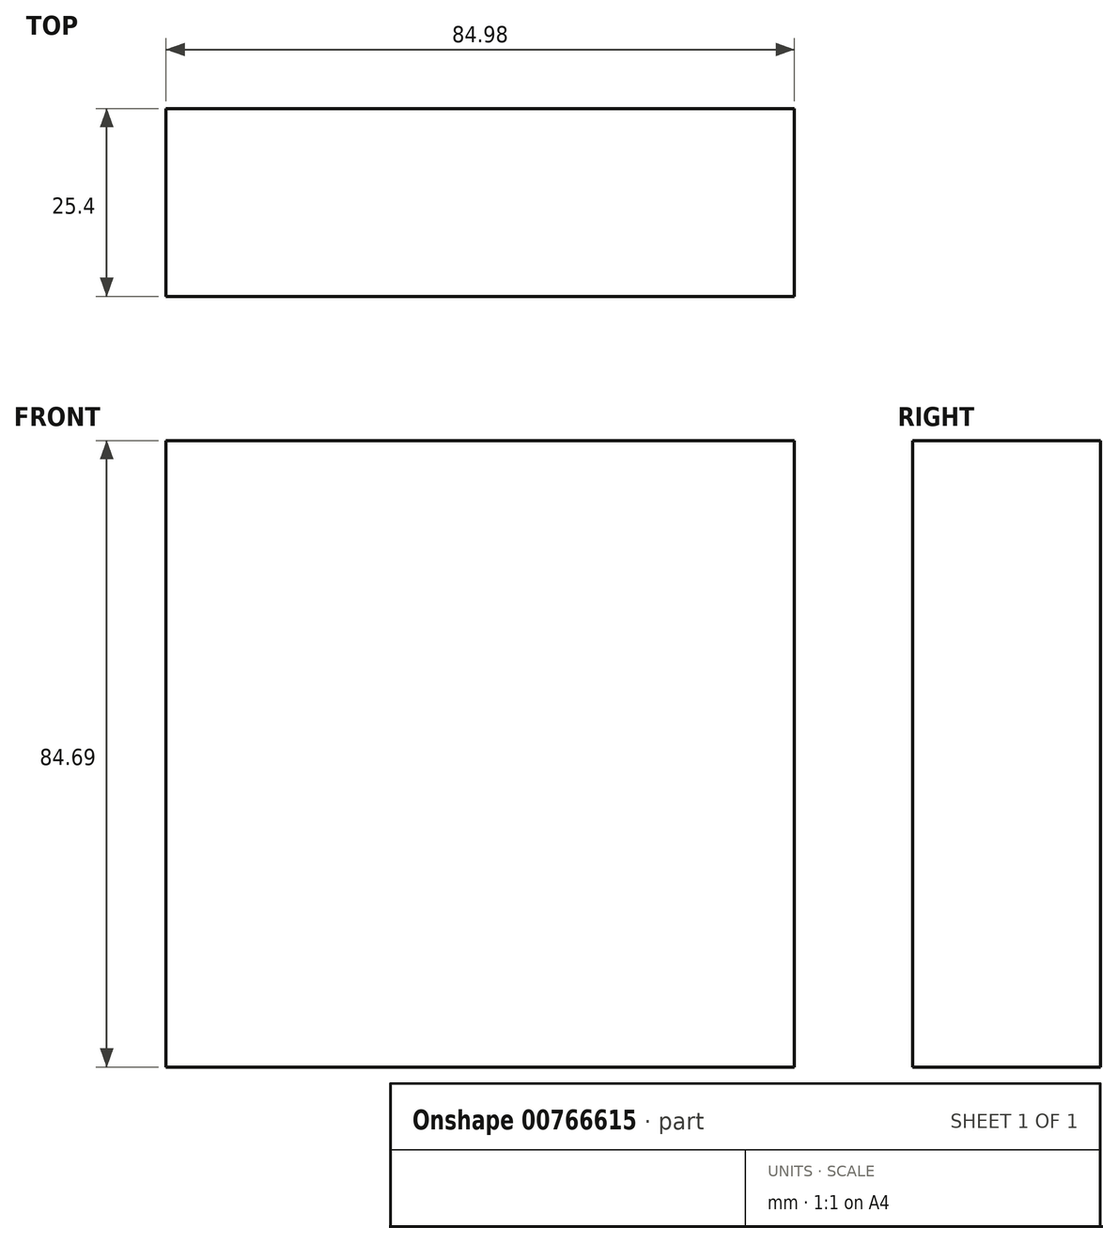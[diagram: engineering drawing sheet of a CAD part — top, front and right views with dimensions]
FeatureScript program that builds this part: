
annotation { "Feature Type Name" : "Feature", "Feature Type Description" : "" }
export const myFeature = defineFeature(function(context is Context, id is Id, definition is map)
    precondition{}
    {
        {
            var Q0;
            Q0=qCreatedBy(makeId("Front.planeOp"),FACE);
            var sketch = newSketch(context, id + "F0", { "sketchPlane" : qUnion([Q0])});
            skLineSegment(sketch, "E0.bottom", {"start": v(-42.49, 26.43) * mm, "end": v(42.49, 26.43) * mm});
            skLineSegment(sketch, "E0.top", {"start": v(-42.49, -58.26) * mm, "end": v(42.49, -58.26) * mm});
            skLineSegment(sketch, "E0.left", {"start": v(-42.49, 26.43) * mm, "end": v(-42.49, -58.26) * mm});
            skLineSegment(sketch, "E0.right", {"start": v(42.49, 26.43) * mm, "end": v(42.49, -58.26) * mm});
            skSolve(sketch);
        }
        {
            var Q0;
            Q0=makeQuery(id+"F0.imprint","IMPRINT",FACE,{"disambiguationData":[TD([[makeQuery(id+"F0.imprint","IMPRINT",EDGE,{"derivedFrom":sQuery(id+"F0.wireOp",EDGE,"E0.bottom")}),-1.0]])]});
            extrude(context, id + "F1", {"entities" : qUnion([Q0]), "depth" : 25.4 * mm, "offsetDistance" : 25.4 * mm});
        }
    });
